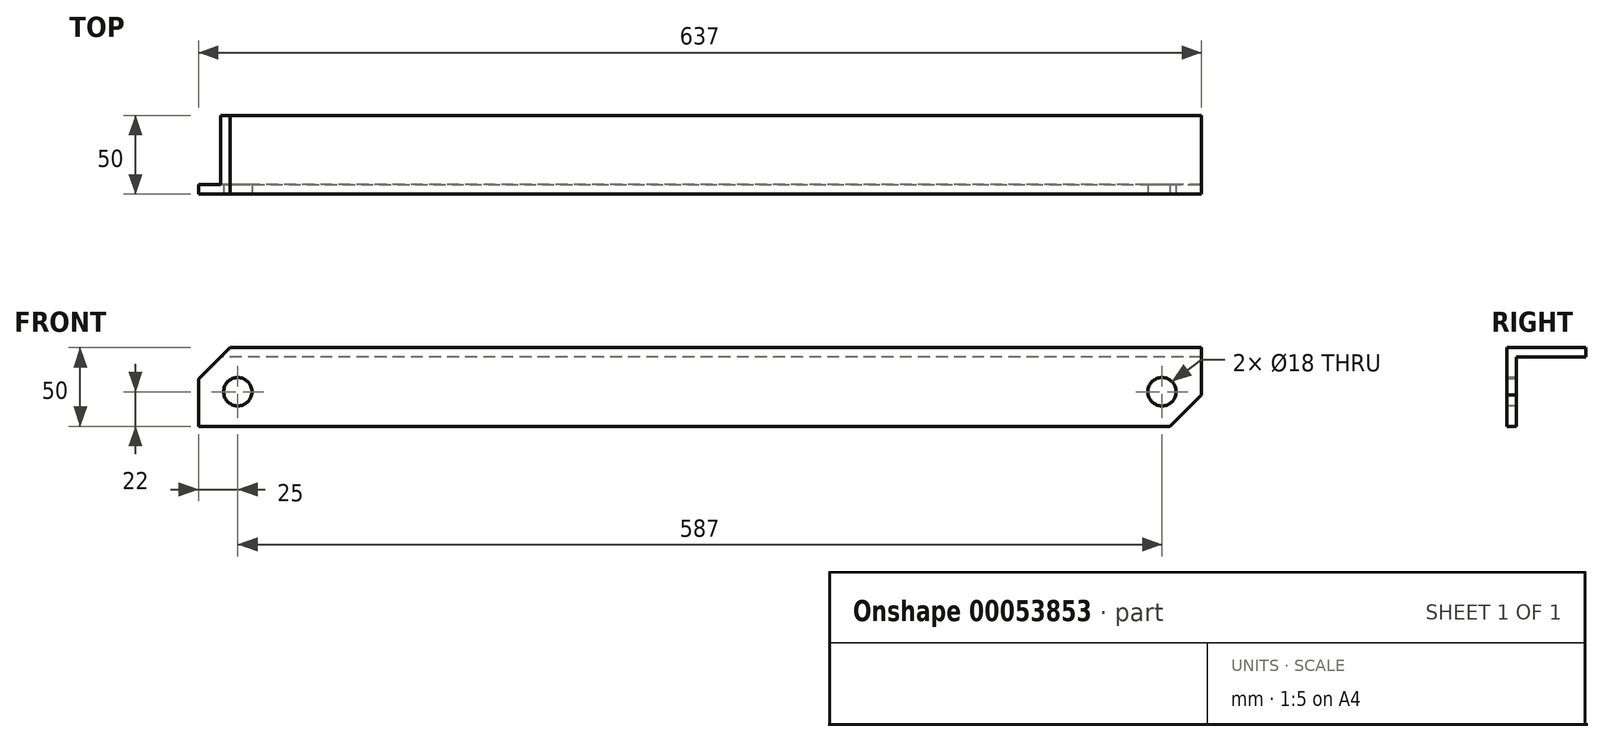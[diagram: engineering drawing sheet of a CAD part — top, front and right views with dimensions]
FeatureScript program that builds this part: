
annotation { "Feature Type Name" : "Feature", "Feature Type Description" : "" }
export const myFeature = defineFeature(function(context is Context, id is Id, definition is map)
    precondition{}
    {
        {
            var Q0;
            Q0=qCreatedBy(makeId("Front.planeOp"),FACE);
            var sketch = newSketch(context, id + "F0", { "sketchPlane" : qUnion([Q0])});
            skLineSegment(sketch, "E0.bottom", {"start": v(0, 0) * mm, "end": v(637, 0) * mm});
            skLineSegment(sketch, "E0.top", {"start": v(0, 50) * mm, "end": v(637, 50) * mm});
            skLineSegment(sketch, "E0.left", {"start": v(0, 0) * mm, "end": v(0, 50) * mm});
            skLineSegment(sketch, "E0.right", {"start": v(637, 0) * mm, "end": v(637, 50) * mm});
            skSolve(sketch);
        }
        {
            var Q0;
            Q0 = qSketchRegion(id + "F0", true);
            extrude(context, id + "F1", {"entities" : qUnion([Q0]), "depth" : 6 * mm});
        }
        {
            var Q0;
            Q0=makeQuery(id+"F1.opExtrude","CAP_FACE",FACE,{"disambiguationData":[OSD([sQuery(id+"F0.wireOp",EDGE,"E0.bottom"),sQuery(id+"F0.wireOp",EDGE,"E0.top"),sQuery(id+"F0.wireOp",EDGE,"E0.left"),sQuery(id+"F0.wireOp",EDGE,"E0.right")])],"isStart":true});
            var sketch = newSketch(context, id + "F2", { "sketchPlane" : qUnion([Q0])});
            skLineSegment(sketch, "E1.bottom", {"start": v(-637, 50) * mm, "end": v(0, 50) * mm});
            skLineSegment(sketch, "E1.top", {"start": v(-637, 44) * mm, "end": v(0, 44) * mm});
            skLineSegment(sketch, "E1.left", {"start": v(-637, 50) * mm, "end": v(-637, 44) * mm});
            skLineSegment(sketch, "E1.right", {"start": v(0, 50) * mm, "end": v(0, 44) * mm});
            skSolve(sketch);
        }
        {
            var Q0;
            Q0 = qSketchRegion(id + "F2", true);
            extrude(context, id + "F3", {"entities" : qUnion([Q0]), "operationType" : NewBodyOperationType.ADD, "depth" : 44 * mm});
        }
        {
            var Q0;
            Q0=makeQuery(id+"F1.opExtrude","CAP_FACE",FACE,{"disambiguationData":[OSD([sQuery(id+"F0.wireOp",EDGE,"E0.bottom"),sQuery(id+"F0.wireOp",EDGE,"E0.top"),sQuery(id+"F0.wireOp",EDGE,"E0.left"),sQuery(id+"F0.wireOp",EDGE,"E0.right")])],"isStart":false});
            var sketch = newSketch(context, id + "F4", { "sketchPlane" : qUnion([Q0])});
            skCircle(sketch, "E2", {"center": v(25, 22) * mm, "radius": 9 * mm});
            skCircle(sketch, "E3", {"center": v(612, 22) * mm, "radius": 9 * mm});
            skSolve(sketch);
        }
        {
            var Q0;
            Q0=makeQuery(id+"F4.imprint","IMPRINT",FACE,{"disambiguationData":[TD([[makeQuery(id+"F4.imprint","IMPRINT",EDGE,{"derivedFrom":sQuery(id+"F4.wireOp",EDGE,"E2")}),1.0]])]});
            var Q1;
            Q1=makeQuery(id+"F4.imprint","IMPRINT",FACE,{"disambiguationData":[TD([[makeQuery(id+"F4.imprint","IMPRINT",EDGE,{"derivedFrom":sQuery(id+"F4.wireOp",EDGE,"E3")}),1.0]])]});
            extrude(context, id + "F5", {"entities" : qUnion([Q0, Q1]), "operationType" : NewBodyOperationType.REMOVE, "oppositeDirection" : true, "depth" : 25 * mm});
        }
        {
            var Q0;
            Q0=makeQuery(id+"F1.opExtrude","CAP_FACE",FACE,{"disambiguationData":[OSD([sQuery(id+"F0.wireOp",EDGE,"E0.bottom"),sQuery(id+"F0.wireOp",EDGE,"E0.top"),sQuery(id+"F0.wireOp",EDGE,"E0.left"),sQuery(id+"F0.wireOp",EDGE,"E0.right")])],"isStart":false});
            var sketch = newSketch(context, id + "F6", { "sketchPlane" : qUnion([Q0])});
            skLineSegment(sketch, "E4", {"start": v(0, 30) * mm, "end": v(20, 50) * mm});
            skLineSegment(sketch, "E5", {"start": v(617, 0) * mm, "end": v(637, 20) * mm});
            skSolve(sketch);
        }
        {
            var Q0;
            {var subQ0=sQuery(id+"F6.wireOp",EDGE,"E5");Q0=makeQuery(id+"F6.imprint","IMPRINT",FACE,{"disambiguationData":[TD([[makeQuery(id+"F6.imprint","IMPRINT",EDGE,{"derivedFrom":subQ0}),-1.0]])]});}
            var Q1;
            {var subQ0=sQuery(id+"F6.wireOp",EDGE,"E4");Q1=makeQuery(id+"F6.imprint","IMPRINT",FACE,{"disambiguationData":[TD([[makeQuery(id+"F6.imprint","IMPRINT",EDGE,{"derivedFrom":subQ0}),1.0]])]});}
            extrude(context, id + "F7", {"entities" : qUnion([Q0, Q1]), "operationType" : NewBodyOperationType.REMOVE, "oppositeDirection" : true, "depth" : 50 * mm});
        }
    });
